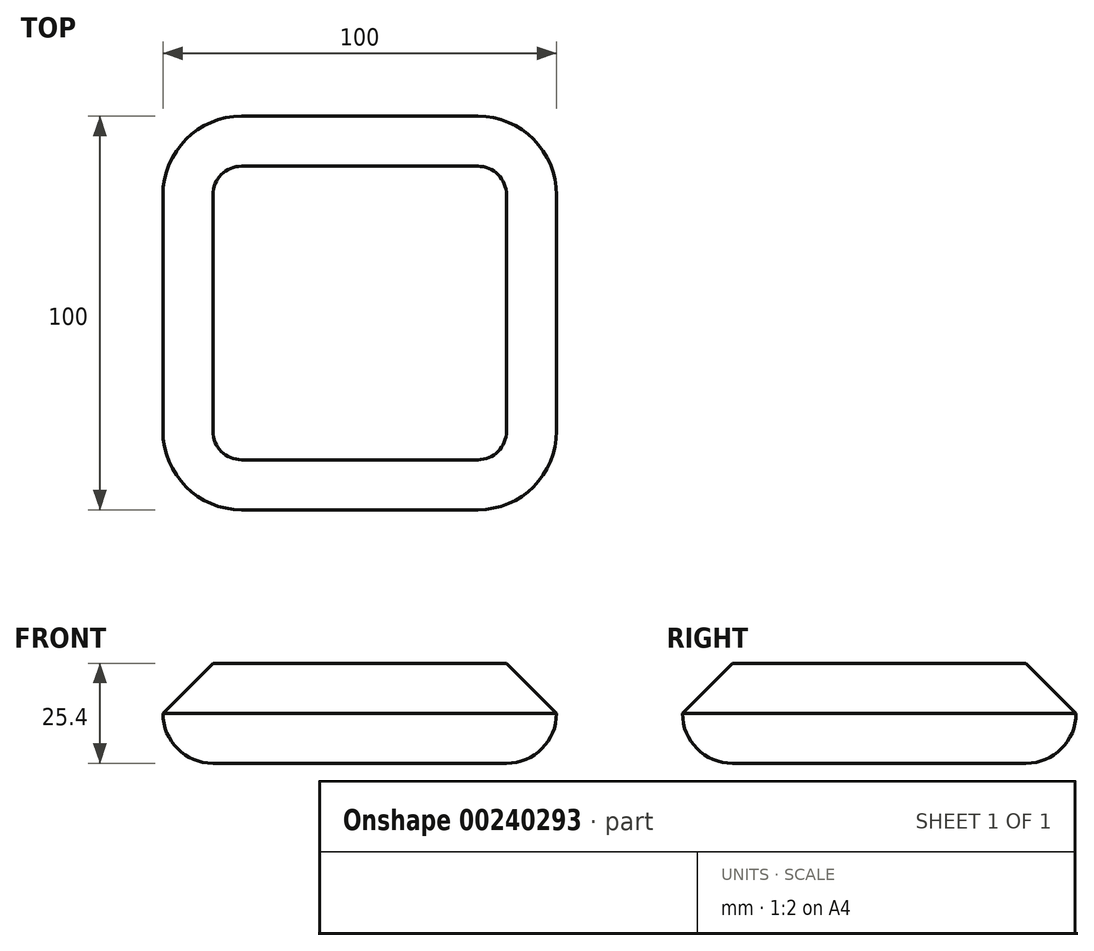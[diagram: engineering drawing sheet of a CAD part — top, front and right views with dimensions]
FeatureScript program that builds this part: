
annotation { "Feature Type Name" : "Feature", "Feature Type Description" : "" }
export const myFeature = defineFeature(function(context is Context, id is Id, definition is map)
    precondition{}
    {
        {
            var Q0;
            Q0=qCreatedBy(makeId("Top.planeOp"),FACE);
            var sketch = newSketch(context, id + "F0", { "sketchPlane" : qUnion([Q0])});
            skLineSegment(sketch, "E0.bottom", {"start": v(-30, -50) * mm, "end": v(30, -50) * mm});
            skLineSegment(sketch, "E0.top", {"start": v(-30, 50) * mm, "end": v(30, 50) * mm});
            skLineSegment(sketch, "E0.left", {"start": v(-50, -30) * mm, "end": v(-50, 30) * mm});
            skLineSegment(sketch, "E0.right", {"start": v(50, -30) * mm, "end": v(50, 30) * mm});
            skPoint(sketch, "E0.middle", {"position": v(0, 0) * mm});
            skPoint(sketch, "E1.visualSharp", {"position": v(-50, 50) * mm});
            skArc(sketch, "E1.filletArc", {"start": v(-30, 50) * mm, "mid": v(-44.14, 44.14) * mm, "end": v(-50, 30) * mm});
            skPoint(sketch, "E2.visualSharp", {"position": v(50, 50) * mm});
            skArc(sketch, "E2.filletArc", {"start": v(50, 30) * mm, "mid": v(44.14, 44.14) * mm, "end": v(30, 50) * mm});
            skPoint(sketch, "E3.visualSharp", {"position": v(50, -50) * mm});
            skArc(sketch, "E3.filletArc", {"start": v(30, -50) * mm, "mid": v(44.14, -44.14) * mm, "end": v(50, -30) * mm});
            skPoint(sketch, "E4.visualSharp", {"position": v(-50, -50) * mm});
            skArc(sketch, "E4.filletArc", {"start": v(-50, -30) * mm, "mid": v(-44.14, -44.14) * mm, "end": v(-30, -50) * mm});
            skSolve(sketch);
        }
        {
            var Q0;
            Q0=makeQuery(id+"F0.imprint","IMPRINT",FACE,{"disambiguationData":[TD([[makeQuery(id+"F0.imprint","IMPRINT",EDGE,{"derivedFrom":sQuery(id+"F0.wireOp",EDGE,"E0.bottom")}),1.0]])]});
            extrude(context, id + "F1", {"entities" : qUnion([Q0]), "depth" : 25.4 * mm});
        }
        {
            var Q0;
            Q0=makeQuery(id+"F1.opExtrude","CAP_FACE",FACE,{"disambiguationData":[OSD([sQuery(id+"F0.wireOp",EDGE,"E0.bottom"),sQuery(id+"F0.wireOp",EDGE,"E0.top"),sQuery(id+"F0.wireOp",EDGE,"E0.left"),sQuery(id+"F0.wireOp",EDGE,"E0.right"),sQuery(id+"F0.wireOp",EDGE,"E1.filletArc"),sQuery(id+"F0.wireOp",EDGE,"E2.filletArc"),sQuery(id+"F0.wireOp",EDGE,"E3.filletArc"),sQuery(id+"F0.wireOp",EDGE,"E4.filletArc")])],"isStart":true});
            fillet(context, id + "F2", {"entities" : qUnion([Q0]), "radius" : 12.7 * mm, "tangentPropagation" : true, "allowEdgeOverflow" : false});
        }
        {
            var Q0;
            Q0=makeQuery(id+"F1.opExtrude","CAP_FACE",FACE,{"disambiguationData":[OSD([sQuery(id+"F0.wireOp",EDGE,"E0.bottom"),sQuery(id+"F0.wireOp",EDGE,"E0.top"),sQuery(id+"F0.wireOp",EDGE,"E0.left"),sQuery(id+"F0.wireOp",EDGE,"E0.right"),sQuery(id+"F0.wireOp",EDGE,"E1.filletArc"),sQuery(id+"F0.wireOp",EDGE,"E2.filletArc"),sQuery(id+"F0.wireOp",EDGE,"E3.filletArc"),sQuery(id+"F0.wireOp",EDGE,"E4.filletArc")])],"isStart":false});
            chamfer(context, id + "F3", {"entities" : qUnion([Q0]), "width" : 12.7 * mm, "tangentPropagation" : true});
        }
    });
